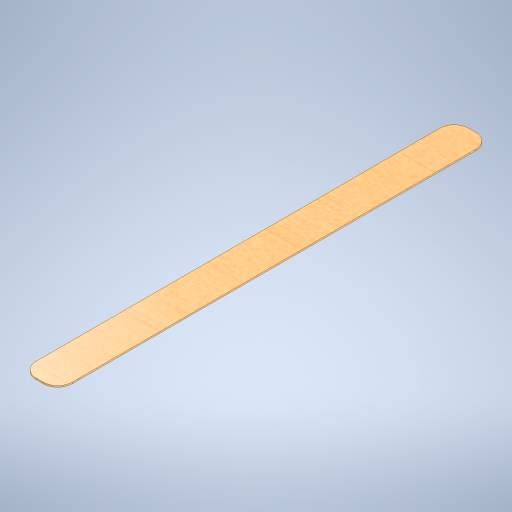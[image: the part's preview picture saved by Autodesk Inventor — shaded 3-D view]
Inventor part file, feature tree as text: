
AUTODESK INVENTOR PART (.ipt)
format: ipt  version: 2023 (Build 270158000, 158)  size: 274,944 bytes
history: native  units: in
note: dims shown in document units (in); Inventor stores cm internally (conversion verified against a paired STEP export)
features: extrude x1, sketch x1
ambient origin geometry x8: Origin, YZ Plane, XZ Plane, XY Plane, X Axis, Y Axis, Z Axis, Center Point
bodies: Solid1 (feature_tree)
feature tree (2):
  extrude  "Extrusion1"  Depth=11.811in
  sketch  "Sketch1"  dims[d0=0.9843in d1=11.811in d2=0.0787in d3=0.3937in d4=0.0394in d5=0.0in]
